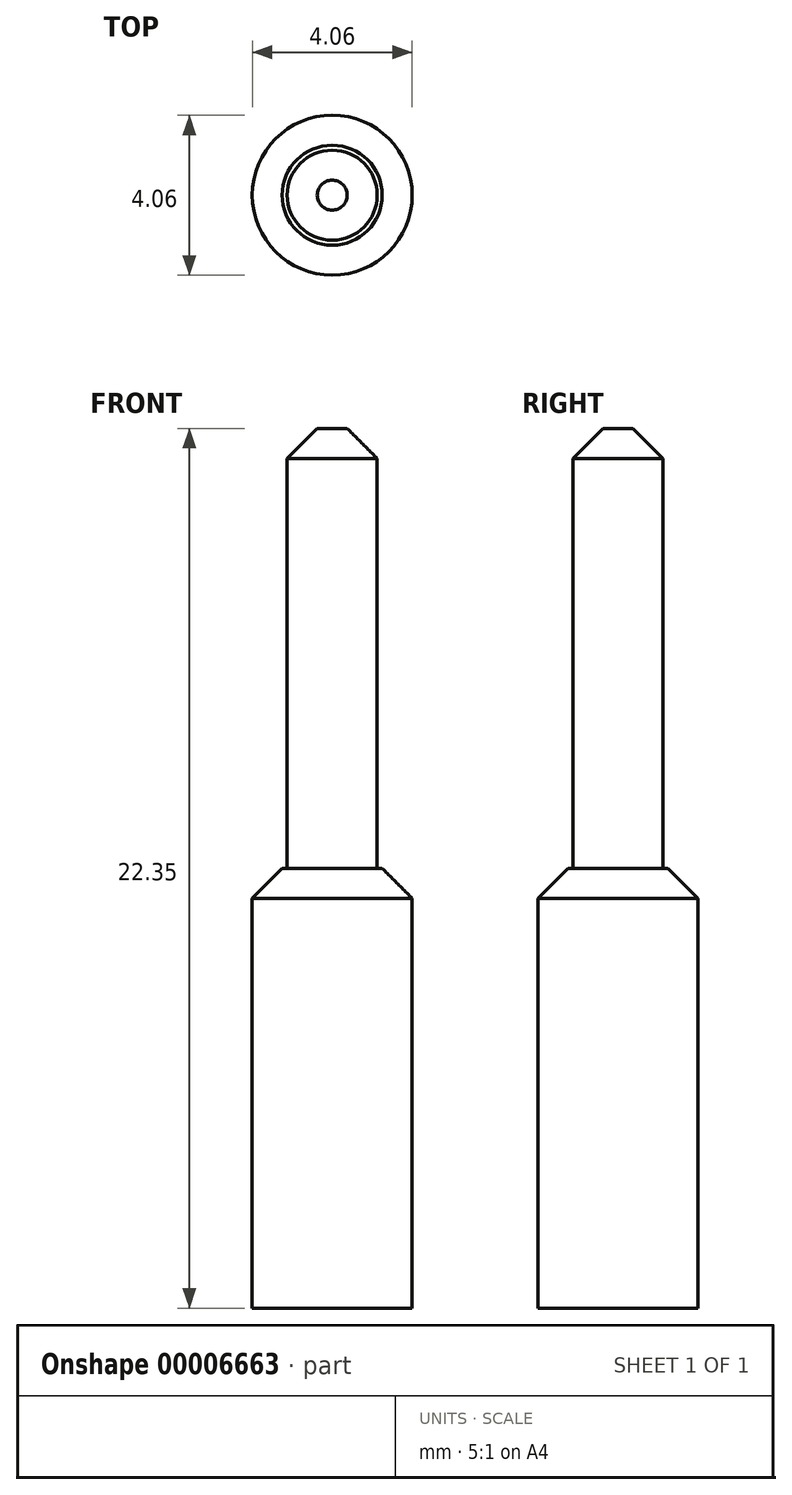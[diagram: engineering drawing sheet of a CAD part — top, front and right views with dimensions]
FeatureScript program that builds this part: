
annotation { "Feature Type Name" : "Feature", "Feature Type Description" : "" }
export const myFeature = defineFeature(function(context is Context, id is Id, definition is map)
    precondition{}
    {
        {
            var Q0;
            Q0=qCreatedBy(makeId("Top.planeOp"),FACE);
            var sketch = newSketch(context, id + "F0", { "sketchPlane" : qUnion([Q0])});
            skCircle(sketch, "E0", {"center": v(0, 0) * mm, "radius": 2.03 * mm});
            skSolve(sketch);
        }
        {
            var Q0;
            Q0 = qSketchRegion(id + "F0", true);
            extrude(context, id + "F1", {"entities" : qUnion([Q0]), "depth" : 11.18 * mm});
        }
        {
            var Q0;
            Q0=makeQuery(id+"F1.opExtrude","CAP_FACE",FACE,{"disambiguationData":[OSD([sQuery(id+"F0.wireOp",EDGE,"E0")])],"isStart":false});
            var sketch = newSketch(context, id + "F2", { "sketchPlane" : qUnion([Q0])});
            skCircle(sketch, "E1", {"center": v(0, 0) * mm, "radius": 1.14 * mm});
            skSolve(sketch);
        }
        {
            var Q0;
            Q0 = qSketchRegion(id + "F2", true);
            extrude(context, id + "F3", {"entities" : qUnion([Q0]), "operationType" : NewBodyOperationType.ADD, "depth" : 11.18 * mm});
        }
        {
            var Q0;
            Q0=makeQuery(id+"F1.opExtrude","CAP_EDGE",EDGE,{"disambiguationData":[OSD([sQuery(id+"F0.wireOp",EDGE,"E0")])],"isStart":false});
            chamfer(context, id + "F4", {"entities" : qUnion([Q0]), "chamferType" : ChamferType.OFFSET_ANGLE, "width" : 0.76 * mm, "oppositeDirection" : false, "angle" : 45 * degree, "tangentPropagation" : true});
        }
        {
            var Q0;
            Q0=makeQuery(id+"F3.opExtrude","CAP_EDGE",EDGE,{"disambiguationData":[OSD([sQuery(id+"F2.wireOp",EDGE,"E1")])],"isStart":false});
            chamfer(context, id + "F5", {"entities" : qUnion([Q0]), "width" : 0.76 * mm, "tangentPropagation" : true});
        }
    });
